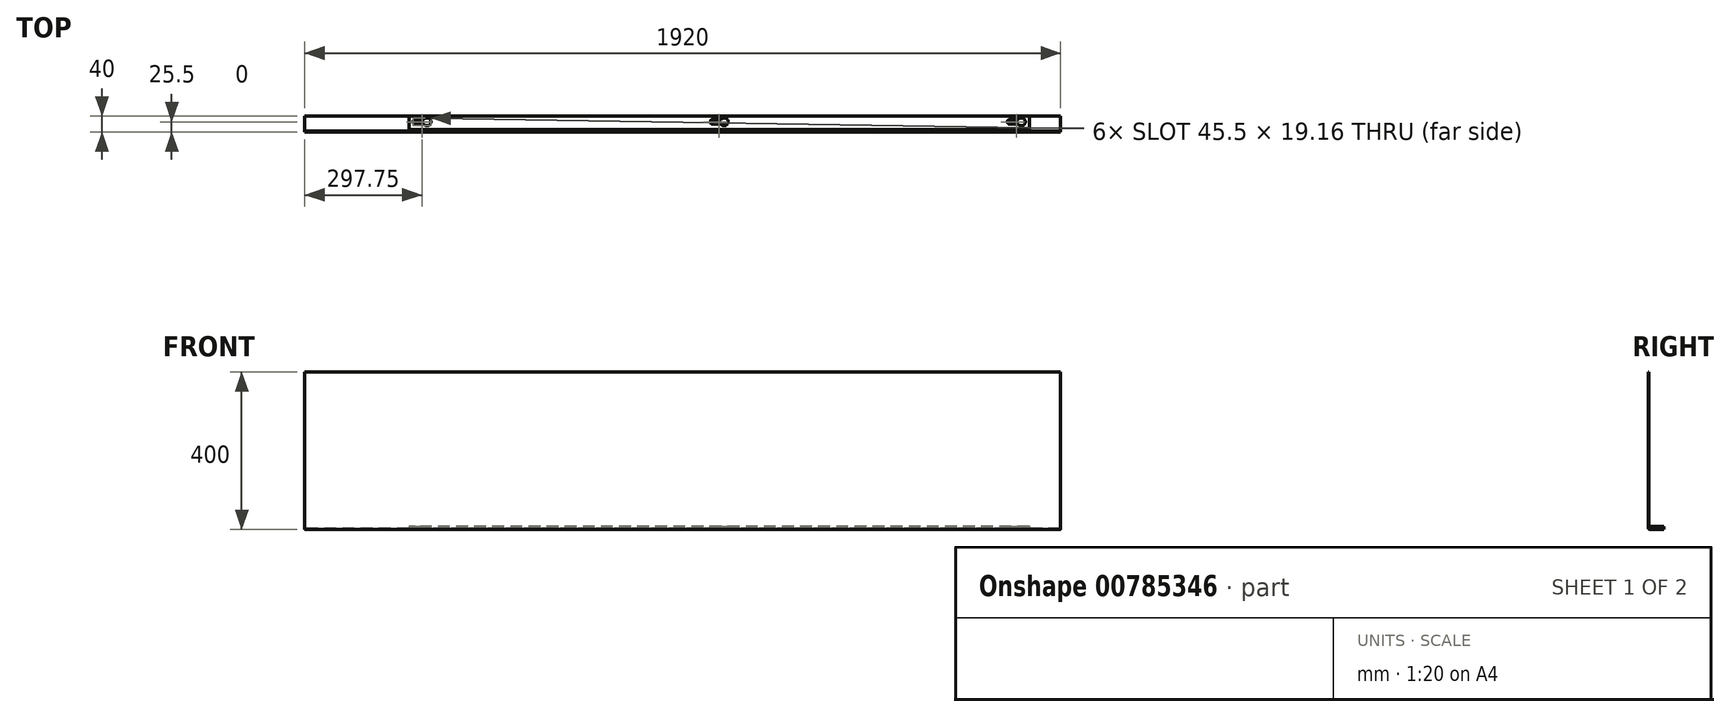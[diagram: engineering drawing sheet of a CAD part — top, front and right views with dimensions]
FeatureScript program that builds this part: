
annotation { "Feature Type Name" : "Feature", "Feature Type Description" : "" }
export const myFeature = defineFeature(function(context is Context, id is Id, definition is map)
    precondition{}
    {
        {
            var Q0;
            Q0=qCreatedBy(makeId("Right.planeOp"),FACE);
            var sketch = newSketch(context, id + "F0", { "sketchPlane" : qUnion([Q0])});
            skLineSegment(sketch, "E0", {"start": v(0, 234.32) * mm, "end": v(0, -161.68) * mm});
            skLineSegment(sketch, "E1", {"start": v(4, -165.68) * mm, "end": v(40, -165.68) * mm});
            skPoint(sketch, "E2.visualSharp", {"position": v(0, -165.68) * mm});
            skArc(sketch, "E2.filletArc", {"start": v(0, -161.68) * mm, "mid": v(1.17, -164.5) * mm, "end": v(4, -165.68) * mm});
            skLineSegment(sketch, "E3.0", {"start": v(4, -163.68) * mm, "end": v(40, -163.68) * mm});
            skArc(sketch, "E3.1", {"start": v(2, -161.68) * mm, "mid": v(2.59, -163.1) * mm, "end": v(4, -163.68) * mm});
            skLineSegment(sketch, "E3.2", {"start": v(2, 234.32) * mm, "end": v(2, -161.68) * mm});
            skLineSegment(sketch, "E4", {"start": v(0, 234.32) * mm, "end": v(2, 234.32) * mm});
            skLineSegment(sketch, "E5", {"start": v(40, -165.68) * mm, "end": v(40, -163.68) * mm});
            skSolve(sketch);
        }
        {
            var Q0;
            Q0=makeQuery(id+"F0.imprint","IMPRINT",FACE,{"disambiguationData":[TD([[makeQuery(id+"F0.imprint","IMPRINT",EDGE,{"derivedFrom":sQuery(id+"F0.wireOp",EDGE,"E0")}),1.0]])]});
            extrude(context, id + "F1", {"entities" : qUnion([Q0]), "depth" : 1920 * mm, "offsetDistance" : 25 * mm});
        }
        {
            var Q0;
            Q0=makeQuery(id+"F1.opExtrude","SWEPT_FACE",FACE,{"disambiguationData":[OSD([sQuery(id+"F0.wireOp",EDGE,"E3.0")])]});
            var sketch = newSketch(context, id + "F2", { "sketchPlane" : qUnion([Q0])});
            skArc(sketch, "E6", {"start": v(1812.15, 20) * mm, "mid": v(1830.5, 25.5) * mm, "end": v(1812.15, 31) * mm});
            skArc(sketch, "E7", {"start": v(1790.5, 31) * mm, "mid": v(1785, 25.5) * mm, "end": v(1790.5, 20) * mm});
            skLineSegment(sketch, "E8", {"start": v(1790.5, 20) * mm, "end": v(1812.15, 20) * mm});
            skLineSegment(sketch, "E9", {"start": v(1790.5, 31) * mm, "end": v(1812.15, 31) * mm});
            skArc(sketch, "E10.1.0.0", {"start": v(1057.15, 20) * mm, "mid": v(1075.5, 25.5) * mm, "end": v(1057.15, 31) * mm});
            skLineSegment(sketch, "E10.1.0.1", {"start": v(1035.5, 31) * mm, "end": v(1057.15, 31) * mm});
            skArc(sketch, "E10.1.0.2", {"start": v(1035.5, 31) * mm, "mid": v(1030, 25.5) * mm, "end": v(1035.5, 20) * mm});
            skLineSegment(sketch, "E10.1.0.3", {"start": v(1035.5, 20) * mm, "end": v(1057.15, 20) * mm});
            skArc(sketch, "E10.2.0.0", {"start": v(302.15, 20) * mm, "mid": v(320.5, 25.5) * mm, "end": v(302.15, 31) * mm});
            skLineSegment(sketch, "E10.2.0.1", {"start": v(280.5, 31) * mm, "end": v(302.15, 31) * mm});
            skArc(sketch, "E10.2.0.2", {"start": v(280.5, 31) * mm, "mid": v(275, 25.5) * mm, "end": v(280.5, 20) * mm});
            skLineSegment(sketch, "E10.2.0.3", {"start": v(280.5, 20) * mm, "end": v(302.15, 20) * mm});
            skLineSegment(sketch, "E10.direction1", {"start": v(1790.5, 20) * mm, "end": v(1035.5, 20) * mm, "construction": true});
            skSolve(sketch);
        }
        {
            var Q0;
            Q0=makeQuery(id+"F2.imprint","IMPRINT",FACE,{"disambiguationData":[TD([[makeQuery(id+"F2.imprint","IMPRINT",EDGE,{"derivedFrom":sQuery(id+"F2.wireOp",EDGE,"E6")}),-1.0]])]});
            var sketch = newSketch(context, id + "F3", { "sketchPlane" : qUnion([Q0])});
            skLineSegment(sketch, "E11", {"start": v(1840.5, 40) * mm, "end": v(1840.5, 6) * mm});
            skLineSegment(sketch, "E12", {"start": v(265, 40) * mm, "end": v(265, 6) * mm});
            skLineSegment(sketch, "E13", {"start": v(265, 6) * mm, "end": v(1840.5, 6) * mm});
            skLineSegment(sketch, "E14", {"start": v(1840.5, 40) * mm, "end": v(265, 40) * mm});
            skSolve(sketch);
        }
        {
            var Q0;
            Q0 = qSketchRegion(id + "F3", true);
            extrude(context, id + "F4", {"entities" : qUnion([Q0]), "depth" : 5 * mm, "offsetDistance" : 25 * mm});
        }
        {
            var Q0;
            Q0 = qSketchRegion(id + "F2", true);
            extrude(context, id + "F5", {"entities" : qUnion([Q0]), "operationType" : NewBodyOperationType.REMOVE, "endBound" : BoundingType.SYMMETRIC, "oppositeDirection" : true, "depth" : 25 * mm, "offsetDistance" : 25 * mm});
        }
        {
            var Q0;
            Q0 = qSketchRegion(id + "F2", true);
            extrude(context, id + "F6", {"entities" : qUnion([Q0]), "operationType" : NewBodyOperationType.REMOVE, "endBound" : BoundingType.SYMMETRIC, "oppositeDirection" : true, "depth" : 25 * mm, "offsetDistance" : 25 * mm});
        }
    });
